# Revit family: Accessory-Teknion-EMOM-Organizers-R2016
name_source: partatom
category: Furniture
revit_build: Autodesk Revit Architecture 2016 (Build: 20150714_1515(x64)
units: mm (PartAtom-declared; Revit-internal decimal feet)

## family parameters
Always vertical = Yes
Cut with Voids When Loaded = No
OmniClass Number = 23.40.20.00
OmniClass Title = General Furniture and Specialties
Room Calculation Point = No
Shared = Yes
Work Plane-Based = Yes

## types (6) — shared parameters
Assembly Code = E2020200
Default Elevation = 48 "
Manufacturer = Teknion
Manufacturer Fax = 416.661.4586
Part Number = EMOM
Product Documentation Link = https://assets.teknion.com
Product Line = Emote
Product Page URL = https://www.teknion.com
Series = Emote
Sustainability Data = https://www.teknion.com
URL = www.teknion.com
Unit Weight URL = http://www.teknion.com
Warranty = http://www.teknion.com

## per-type parameters (varying)
| type | CO | CT | Cork Organizer Depth Offset | Cork Organizer Height Offset | Cork Organizer Width Offset | Depth | Description | Double Medium Tray | LT | Large Tray Feet | M2 | MT | Medium Tray Feet | Medium/Large Tray | Medium/Large Tray Divider | Medium/Large Tray Height Offset | Mini Cabinet Tray | Model | ST | Small Tray | Small Tray Divider Offset | Width |
| Large Tray Bundle | No | No | 13.686 " | 0.209 " | 0.123 " | 24 " | Emote Organizers, Large Tray Bundle | No | Yes | Yes | No | No | No | Yes | Yes | 0.031 " | No | EMOMLT | No | No | 9.755 " | 9.875 " |
| Medium Tray Bundle | No | No | 0.185 " | 0.278 " | 0.122 " | 14.99 " | Emote Organizers, Medium Tray Bundle | No | No | No | No | Yes | Yes | Yes | Yes | 0.039 " | No | EMOMMT | No | No | 9.755 " | 9.875 " |
| Small Tray Bundle | No | No | 0.125 " | 0.217 " | 5.201 " | 3.565 " | Emote Organizers, Small Tray Bundle | No | No | No | No | No | No | No | No | 0.039 " | No | EMOMST | Yes | Yes | 0 " | 14.99 " |
| Mini Cabinet Bundle | No | Yes | 10 " | 0.217 " | 0.161 " | 13.44 " | Emote Organizers, Mini Cabinet Bundle | No | No | No | No | No | No | No | No | 0.039 " | Yes | EMOMCT | No | Yes | 9.755 " | 14.99 " |
| Two Medium Trays | No | No | 0 " | 0 " | 0 " | 14.99 " | Emote Organizers, Two Medium Trays | Yes | No | No | Yes | No | Yes | Yes | No | 0.039 " | No | EMOMM2 | No | No | 9.755 " | 20.75 " |
| Cork Organizer | Yes | No | 0 " | 0 " | 0 " | 3.315 " | Emote Organizers, Cork Organizer | No | No | No | No | No | No | No | No | 0.039 " | No | EMOMCO | No | No | 9.755 " | 9.63 " |

type visibility flags (boolean, named after types; folded from table):
- Large Tray Bundle: Yes: Cork Organizer
- Medium Tray Bundle: Yes: Cork Organizer
- Small Tray Bundle: Yes: Cork Organizer
- Mini Cabinet Bundle: Yes: Cork Organizer
- Two Medium Trays: Yes: (none)
- Cork Organizer: Yes: Cork Organizer

## geometry (parser evidence)
native form markers: Blend x2, Sweep x2
no freeform markers — native parametric forms only
